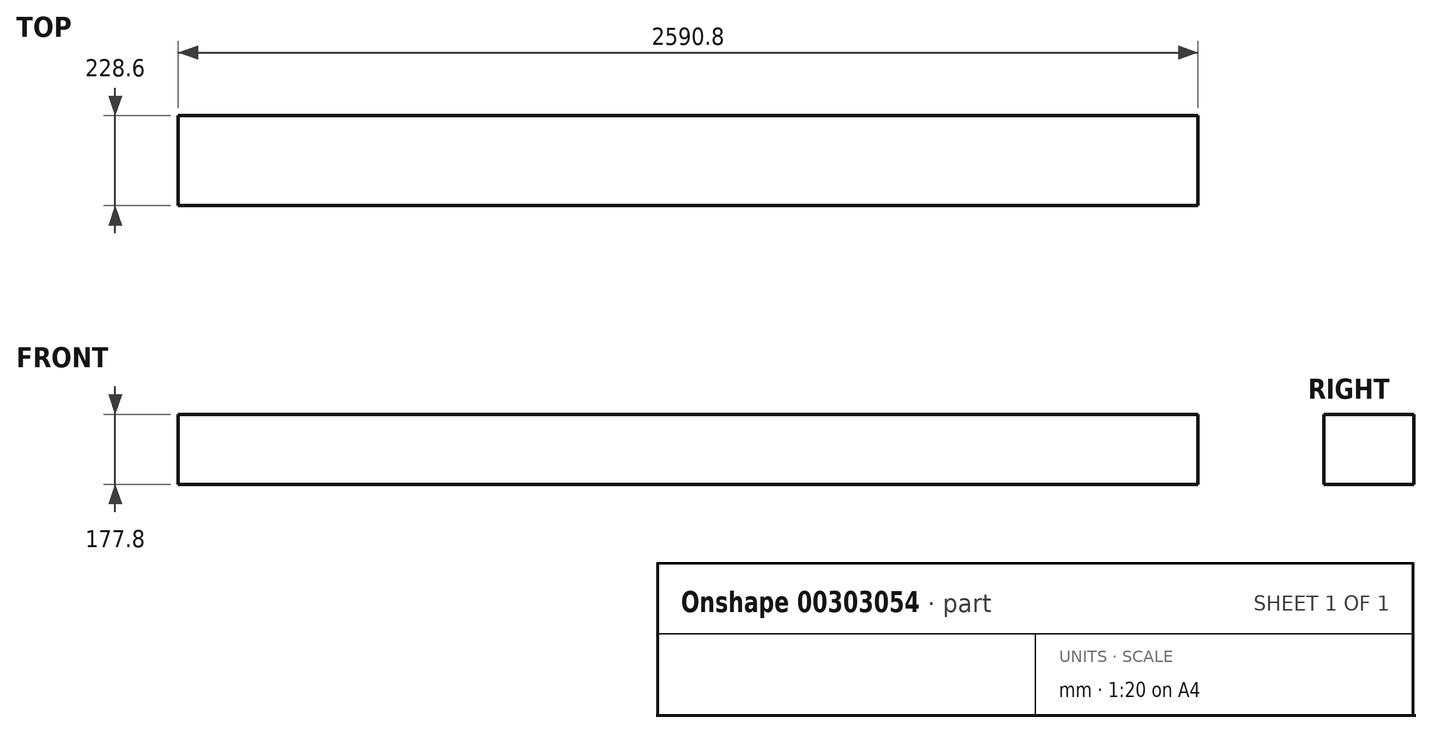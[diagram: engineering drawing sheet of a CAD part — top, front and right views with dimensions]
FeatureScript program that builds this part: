
annotation { "Feature Type Name" : "Feature", "Feature Type Description" : "" }
export const myFeature = defineFeature(function(context is Context, id is Id, definition is map)
    precondition{}
    {
        {
            var Q0;
            Q0=qCreatedBy(makeId("Right.planeOp"),FACE);
            var sketch = newSketch(context, id + "F0", { "sketchPlane" : qUnion([Q0])});
            skLineSegment(sketch, "E0.bottom", {"start": v(114.3, -88.9) * mm, "end": v(-114.3, -88.9) * mm});
            skLineSegment(sketch, "E0.top", {"start": v(114.3, 88.9) * mm, "end": v(-114.3, 88.9) * mm});
            skLineSegment(sketch, "E0.left", {"start": v(114.3, -88.9) * mm, "end": v(114.3, 88.9) * mm});
            skLineSegment(sketch, "E0.right", {"start": v(-114.3, -88.9) * mm, "end": v(-114.3, 88.9) * mm});
            skPoint(sketch, "E0.middle", {"position": v(0, 0) * mm});
            skSolve(sketch);
        }
        {
            var Q0;
            Q0=qSketchRegion(id+"F0",true);
            extrude(context, id + "F1", {"entities" : qUnion([Q0]), "depth" : 2590.8 * mm, "symmetric" : true});
        }
    });
